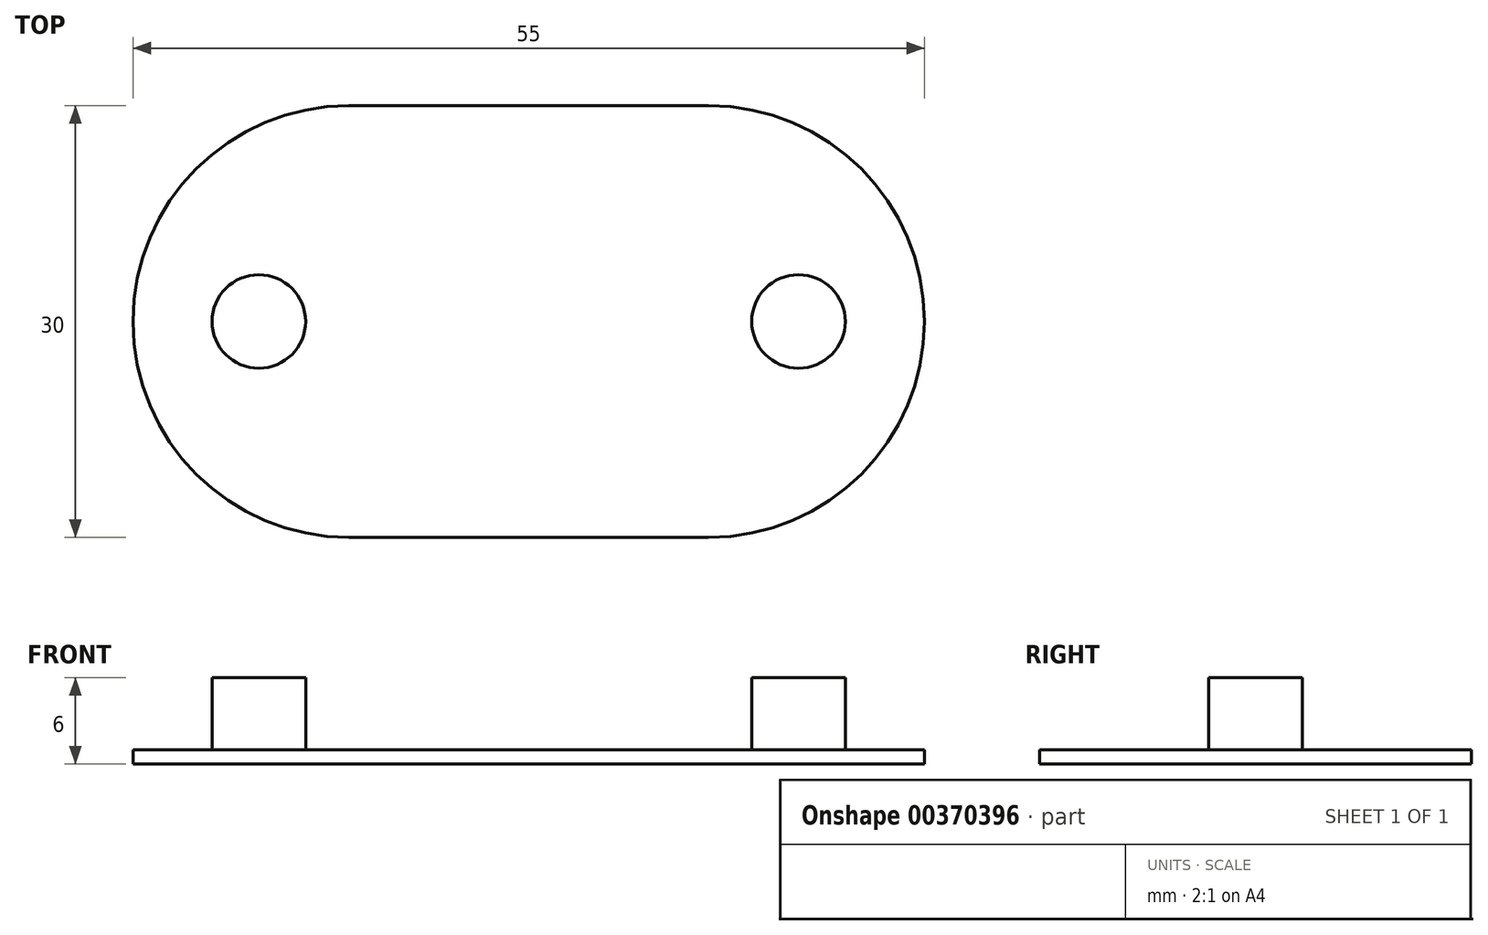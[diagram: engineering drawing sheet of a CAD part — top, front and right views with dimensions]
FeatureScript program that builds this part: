
annotation { "Feature Type Name" : "Feature", "Feature Type Description" : "" }
export const myFeature = defineFeature(function(context is Context, id is Id, definition is map)
    precondition{}
    {
        {
            var Q0;
            Q0=qCreatedBy(makeId("Top.planeOp"),FACE);
            var sketch = newSketch(context, id + "F0", { "sketchPlane" : qUnion([Q0])});
            skArc(sketch, "E0", {"start": v(-12.5, 15) * mm, "mid": v(-27.5, 0) * mm, "end": v(-12.5, -15) * mm});
            skArc(sketch, "E1", {"start": v(12.5, -15) * mm, "mid": v(27.5, 0) * mm, "end": v(12.5, 15) * mm});
            skLineSegment(sketch, "E2", {"start": v(-12.5, 15) * mm, "end": v(12.5, 15) * mm});
            skLineSegment(sketch, "E3", {"start": v(-12.5, -15) * mm, "end": v(12.5, -15) * mm});
            skSolve(sketch);
        }
        {
            var Q0;
            Q0 = qSketchRegion(id + "F0", true);
            extrude(context, id + "F1", {"entities" : qUnion([Q0]), "depth" : 1 * mm});
        }
        {
            var Q0;
            Q0=makeQuery(id+"F1.opExtrude","CAP_FACE",FACE,{"disambiguationData":[OSD([sQuery(id+"F0.wireOp",EDGE,"E0"),sQuery(id+"F0.wireOp",EDGE,"E1"),sQuery(id+"F0.wireOp",EDGE,"E2"),sQuery(id+"F0.wireOp",EDGE,"E3")])],"isStart":false});
            var sketch = newSketch(context, id + "F2", { "sketchPlane" : qUnion([Q0])});
            skCircle(sketch, "E4", {"center": v(-18.75, 0) * mm, "radius": 3.25 * mm});
            skCircle(sketch, "E5", {"center": v(18.75, 0) * mm, "radius": 3.25 * mm});
            skSolve(sketch);
        }
        {
            var Q0;
            Q0 = qSketchRegion(id + "F2", true);
            extrude(context, id + "F3", {"entities" : qUnion([Q0]), "operationType" : NewBodyOperationType.ADD, "depth" : 5 * mm});
        }
    });
